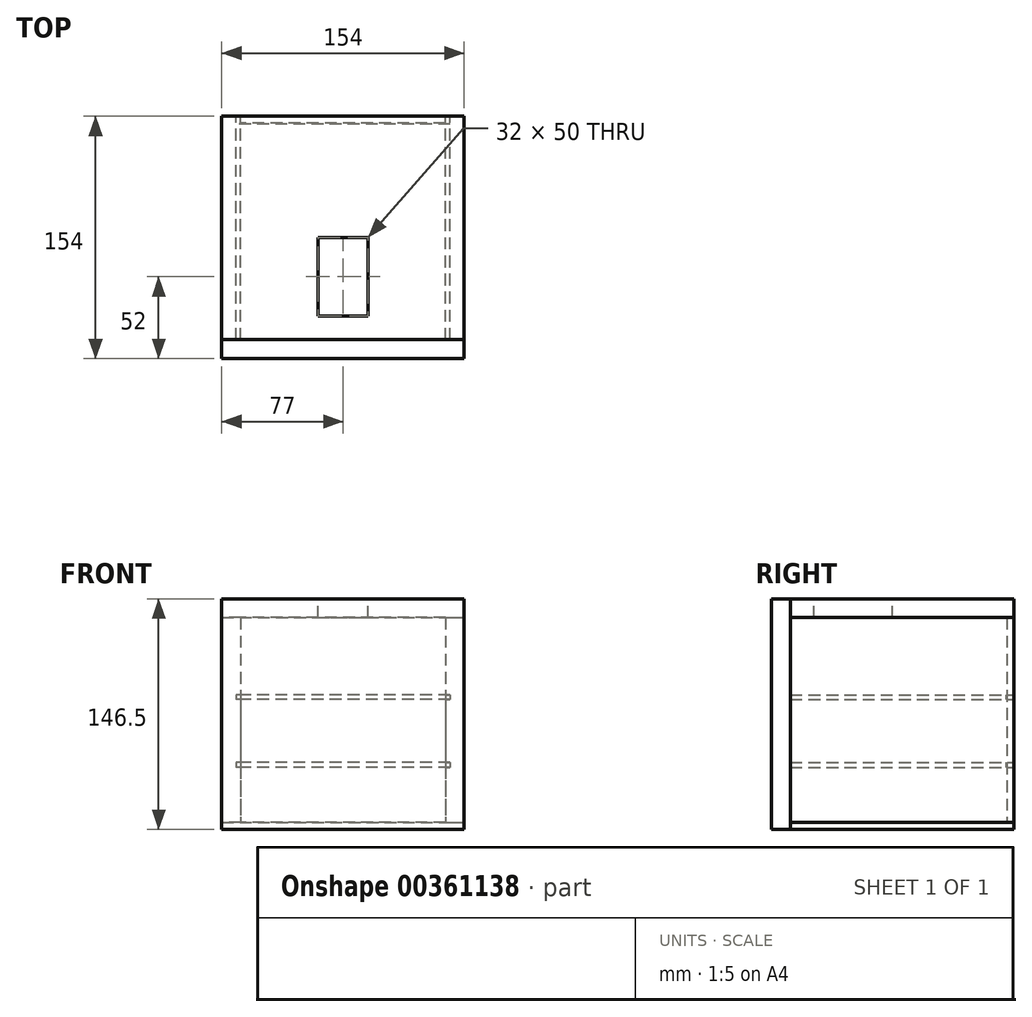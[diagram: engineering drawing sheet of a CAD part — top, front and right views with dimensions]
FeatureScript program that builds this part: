
annotation { "Feature Type Name" : "Feature", "Feature Type Description" : "" }
export const myFeature = defineFeature(function(context is Context, id is Id, definition is map)
    precondition{}
    {
        {
            var Q0;
            Q0=qCreatedBy(makeId("Front.planeOp"),FACE);
            var sketch = newSketch(context, id + "F0", { "sketchPlane" : qUnion([Q0])});
            skLineSegment(sketch, "E0.bottom", {"start": v(-77, 77) * mm, "end": v(77, 77) * mm});
            skLineSegment(sketch, "E0.top", {"start": v(-77, -69.5) * mm, "end": v(77, -69.5) * mm});
            skLineSegment(sketch, "E0.left", {"start": v(-77, 77) * mm, "end": v(-77, -69.5) * mm});
            skLineSegment(sketch, "E0.right", {"start": v(77, 77) * mm, "end": v(77, -69.5) * mm});
            skSolve(sketch);
        }
        {
            var Q0;
            Q0=qSketchRegion(id+"F0",true);
            var Q1;
            Q1=makeQuery(id+"F0.imprint","IMPRINT",FACE,{"disambiguationData":[TD([[makeQuery(id+"F0.imprint","IMPRINT",EDGE,{"derivedFrom":sQuery(id+"F0.wireOp",EDGE,"E0.bottom")}),-1.0]])]});
            extrude(context, id + "F1", {"entities" : qUnion([Q0, Q1]), "depth" : 12 * mm});
        }
        {
            var Q0;
            Q0=makeQuery(id+"F1.opExtrude","SWEPT_FACE",FACE,{"disambiguationData":[OSD([sQuery(id+"F0.wireOp",EDGE,"E0.right")])]});
            var sketch = newSketch(context, id + "F2", { "sketchPlane" : qUnion([Q0])});
            skLineSegment(sketch, "E1.bottom", {"start": v(0, 65) * mm, "end": v(142, 65) * mm});
            skLineSegment(sketch, "E1.top", {"start": v(0, -65) * mm, "end": v(142, -65) * mm});
            skLineSegment(sketch, "E1.left", {"start": v(0, 65) * mm, "end": v(0, -65) * mm});
            skLineSegment(sketch, "E1.right", {"start": v(142, 65) * mm, "end": v(142, -65) * mm});
            skSolve(sketch);
        }
        {
            var Q0;
            Q0=makeQuery(id+"F2.imprint","IMPRINT",FACE,{"disambiguationData":[TD([[makeQuery(id+"F2.imprint","IMPRINT",EDGE,{"derivedFrom":sQuery(id+"F2.wireOp",EDGE,"E1.bottom")}),-1.0]])]});
            extrude(context, id + "F3", {"entities" : qUnion([Q0]), "oppositeDirection" : true, "depth" : 12 * mm});
        }
        {
            var Q0;
            Q0=makeQuery(id+"F1.opExtrude","SWEPT_BODY",BODY,{"disambiguationData":[OSD([sQuery(id+"F0.wireOp",EDGE,"E0.bottom"),sQuery(id+"F0.wireOp",EDGE,"E0.top"),sQuery(id+"F0.wireOp",EDGE,"E0.left"),sQuery(id+"F0.wireOp",EDGE,"E0.right")])]});
            var Q1;
            Q1=qCreatedBy(makeId("Right.planeOp"),FACE);
            mirror(context, id + "F4", {"entities" : qUnion([Q0]), "mirrorPlane" : qUnion([Q1])});
        }
        {
            var Q0;
            Q0=makeQuery(id+"F1.opExtrude","SWEPT_FACE",FACE,{"disambiguationData":[OSD([sQuery(id+"F0.wireOp",EDGE,"E0.bottom")])]});
            var sketch = newSketch(context, id + "F5", { "sketchPlane" : qUnion([Q0])});
            skLineSegment(sketch, "E2.bottom", {"start": v(77, 0) * mm, "end": v(-77, 0) * mm});
            skLineSegment(sketch, "E2.top", {"start": v(77, 142) * mm, "end": v(-77, 142) * mm});
            skLineSegment(sketch, "E2.left", {"start": v(77, 0) * mm, "end": v(77, 142) * mm});
            skLineSegment(sketch, "E2.right", {"start": v(-77, 0) * mm, "end": v(-77, 142) * mm});
            skLineSegment(sketch, "E3.bottom", {"start": v(-16, 65) * mm, "end": v(16, 65) * mm});
            skLineSegment(sketch, "E3.top", {"start": v(-16, 15) * mm, "end": v(16, 15) * mm});
            skLineSegment(sketch, "E3.left", {"start": v(-16, 65) * mm, "end": v(-16, 15) * mm});
            skLineSegment(sketch, "E3.right", {"start": v(16, 65) * mm, "end": v(16, 15) * mm});
            skSolve(sketch);
        }
        {
            var Q0;
            Q0=makeQuery(id+"F5.imprint","IMPRINT",FACE,{"disambiguationData":[TD([[makeQuery(id+"F5.imprint","IMPRINT",EDGE,{"derivedFrom":sQuery(id+"F5.wireOp",EDGE,"E2.bottom")}),1.0]])]});
            extrude(context, id + "F6", {"entities" : qUnion([Q0]), "oppositeDirection" : true, "depth" : 12 * mm});
        }
        {
            var Q0;
            Q0=makeQuery(id+"F1.opExtrude","SWEPT_FACE",FACE,{"disambiguationData":[OSD([sQuery(id+"F0.wireOp",EDGE,"E0.top")])]});
            var sketch = newSketch(context, id + "F7", { "sketchPlane" : qUnion([Q0])});
            skLineSegment(sketch, "E4.bottom", {"start": v(-77, 0) * mm, "end": v(77, 0) * mm});
            skLineSegment(sketch, "E4.top", {"start": v(-77, -142) * mm, "end": v(77, -142) * mm});
            skLineSegment(sketch, "E4.left", {"start": v(-77, 0) * mm, "end": v(-77, -142) * mm});
            skLineSegment(sketch, "E4.right", {"start": v(77, 0) * mm, "end": v(77, -142) * mm});
            skSolve(sketch);
        }
        {
            var Q0;
            Q0=makeQuery(id+"F7.imprint","IMPRINT",FACE,{"disambiguationData":[TD([[makeQuery(id+"F7.imprint","IMPRINT",EDGE,{"derivedFrom":sQuery(id+"F7.wireOp",EDGE,"E4.bottom")}),-1.0]])]});
            extrude(context, id + "F8", {"entities" : qUnion([Q0]), "oppositeDirection" : true, "depth" : 4.5 * mm});
        }
        {
            var Q0;
            Q0=makeQuery(id+"F6.opExtrude","SWEPT_FACE",FACE,{"disambiguationData":[OSD([sQuery(id+"F5.wireOp",EDGE,"E2.top")])]});
            var sketch = newSketch(context, id + "F9", { "sketchPlane" : qUnion([Q0])});
            skLineSegment(sketch, "E5.bottom", {"start": v(-65, 65) * mm, "end": v(65, 65) * mm});
            skLineSegment(sketch, "E5.top", {"start": v(-65, -65) * mm, "end": v(65, -65) * mm});
            skLineSegment(sketch, "E5.left", {"start": v(-65, 65) * mm, "end": v(-65, -65) * mm});
            skLineSegment(sketch, "E5.right", {"start": v(65, 65) * mm, "end": v(65, -65) * mm});
            skSolve(sketch);
        }
        {
            var Q0;
            Q0=makeQuery(id+"F9.imprint","IMPRINT",FACE,{"disambiguationData":[TD([[makeQuery(id+"F9.imprint","IMPRINT",EDGE,{"derivedFrom":sQuery(id+"F9.wireOp",EDGE,"E5.bottom")}),-1.0]])]});
            extrude(context, id + "F10", {"entities" : qUnion([Q0]), "oppositeDirection" : true, "depth" : 4.5 * mm});
        }
        {
            var Q0;
            Q0=makeQuery(id+"F3.opExtrude","SWEPT_FACE",FACE,{"disambiguationData":[OSD([sQuery(id+"F2.wireOp",EDGE,"E1.right")])]});
            var sketch = newSketch(context, id + "F11", { "sketchPlane" : qUnion([Q0])});
            skLineSegment(sketch, "E6.bottom", {"start": v(-65, 16) * mm, "end": v(-68, 16) * mm});
            skLineSegment(sketch, "E6.top", {"start": v(-65, 13) * mm, "end": v(-68, 13) * mm});
            skLineSegment(sketch, "E6.left", {"start": v(-65, 16) * mm, "end": v(-65, 13) * mm});
            skLineSegment(sketch, "E6.right", {"start": v(-68, 16) * mm, "end": v(-68, 13) * mm});
            skLineSegment(sketch, "E7.bottom", {"start": v(-65, -27) * mm, "end": v(-68, -27) * mm});
            skLineSegment(sketch, "E7.top", {"start": v(-65, -30) * mm, "end": v(-68, -30) * mm});
            skLineSegment(sketch, "E7.left", {"start": v(-65, -27) * mm, "end": v(-65, -30) * mm});
            skLineSegment(sketch, "E7.right", {"start": v(-68, -27) * mm, "end": v(-68, -30) * mm});
            skSolve(sketch);
        }
        {
            var Q0;
            Q0=makeQuery(id+"F11.imprint","IMPRINT",FACE,{"disambiguationData":[TD([[makeQuery(id+"F11.imprint","IMPRINT",EDGE,{"derivedFrom":sQuery(id+"F11.wireOp",EDGE,"NvQbIwnB-lqE2-p2Xs-orIO-Tnx0DaEzGyps.bottom")}),1.0]])]});
            var Q1;
            Q1=makeQuery(id+"F11.imprint","IMPRINT",FACE,{"disambiguationData":[TD([[makeQuery(id+"F11.imprint","IMPRINT",EDGE,{"derivedFrom":sQuery(id+"F11.wireOp",EDGE,"E6.bottom")}),1.0]])]});
            var Q2;
            Q2=makeQuery(id+"F11.imprint","IMPRINT",FACE,{"disambiguationData":[TD([[makeQuery(id+"F11.imprint","IMPRINT",EDGE,{"derivedFrom":sQuery(id+"F11.wireOp",EDGE,"E7.bottom")}),1.0]])]});
            extrude(context, id + "F12", {"entities" : qUnion([Q0, Q1, Q2]), "operationType" : NewBodyOperationType.REMOVE, "oppositeDirection" : true, "depth" : 142 * mm});
        }
        {
            var Q0;
            Q0=makeQuery(id+"F3.opExtrude","SWEPT_BODY",BODY,{"disambiguationData":[OSD([sQuery(id+"F2.wireOp",EDGE,"E1.bottom"),sQuery(id+"F2.wireOp",EDGE,"E1.top"),sQuery(id+"F2.wireOp",EDGE,"E1.left"),sQuery(id+"F2.wireOp",EDGE,"E1.right")])]});
            var Q1;
            Q1=qCreatedBy(makeId("Right.planeOp"),FACE);
            mirror(context, id + "F13", {"entities" : qUnion([Q0]), "mirrorPlane" : qUnion([Q1])});
        }
        {
            var Q0;
            Q0=makeQuery(id+"F12.boolean.opBoolean","COPY",FACE,{"derivedFrom":makeQuery(id+"F12.opExtrude","SWEPT_FACE",FACE,{"disambiguationData":[OSD([sQuery(id+"F11.wireOp",EDGE,"E6.top")])]})});
            var sketch = newSketch(context, id + "F14", { "sketchPlane" : qUnion([Q0])});
            skLineSegment(sketch, "E8.bottom", {"start": v(68, 0) * mm, "end": v(-68, 0) * mm});
            skLineSegment(sketch, "E8.top", {"start": v(68, 137) * mm, "end": v(-68, 137) * mm});
            skLineSegment(sketch, "E8.left", {"start": v(68, 0) * mm, "end": v(68, 137) * mm});
            skLineSegment(sketch, "E8.right", {"start": v(-68, 0) * mm, "end": v(-68, 137) * mm});
            skSolve(sketch);
        }
        {
            var Q0;
            Q0=qSketchRegion(id+"F14",true);
            extrude(context, id + "F15", {"entities" : qUnion([Q0]), "depth" : 3 * mm});
        }
        {
            var Q0;
            Q0=makeQuery(id+"F15.opExtrude","SWEPT_BODY",BODY,{"disambiguationData":[OSD([sQuery(id+"F14.wireOp",EDGE,"E8.bottom"),sQuery(id+"F14.wireOp",EDGE,"E8.top"),sQuery(id+"F14.wireOp",EDGE,"E8.left"),sQuery(id+"F14.wireOp",EDGE,"E8.right")])]});
            transform(context, id + "F16", {"entities" : qUnion([Q0]), "transformType" : TransformType.TRANSLATION_3D, "dx" : 0 * mm, "dy" : 0 * mm, "dz" : -43 * mm, "makeCopy" : true});
        }
    });
